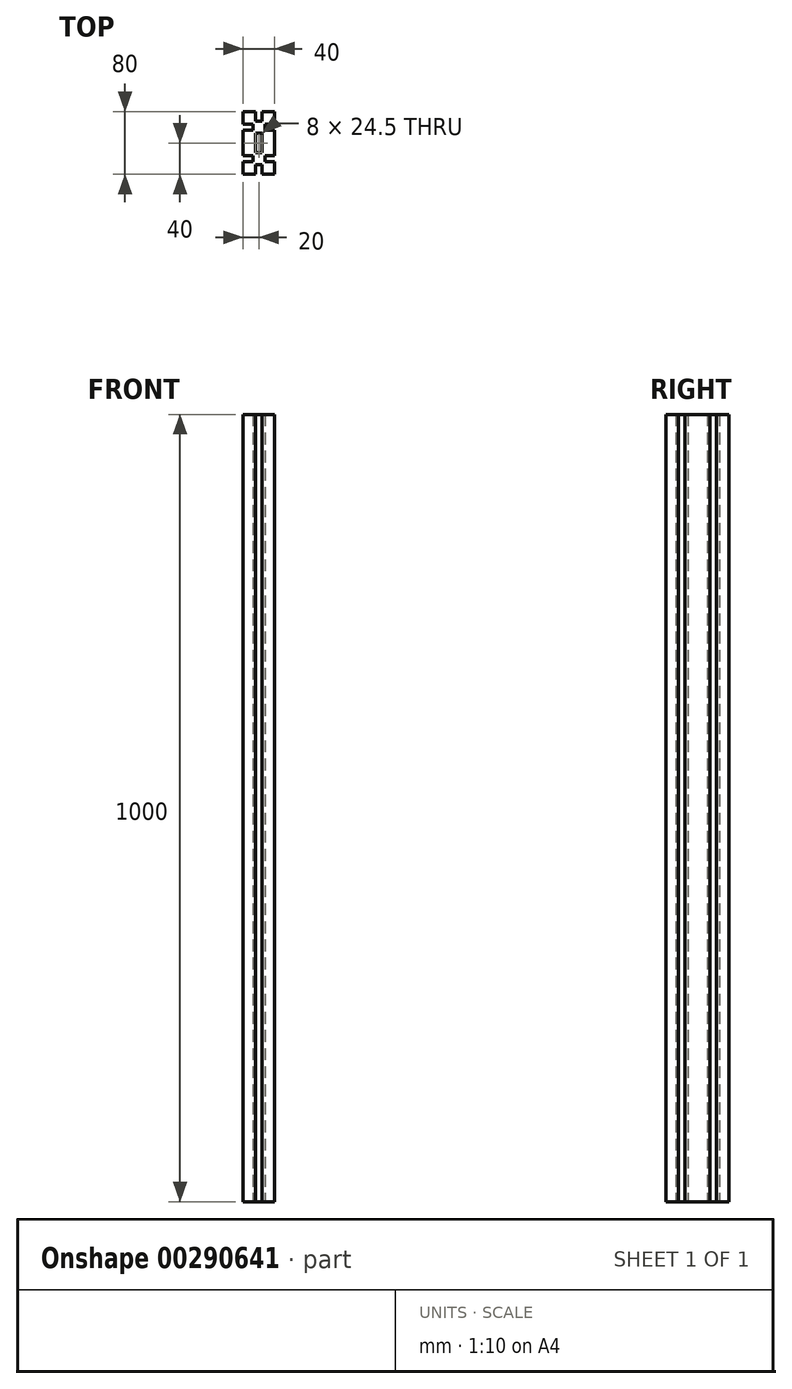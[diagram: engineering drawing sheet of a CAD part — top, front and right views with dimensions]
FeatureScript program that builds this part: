
annotation { "Feature Type Name" : "Feature", "Feature Type Description" : "" }
export const myFeature = defineFeature(function(context is Context, id is Id, definition is map)
    precondition{}
    {
        {
            var Q0;
            Q0=qCreatedBy(makeId("Top.planeOp"),FACE);
            var sketch = newSketch(context, id + "F0", { "sketchPlane" : qUnion([Q0])});
            skLineSegment(sketch, "E0.bottom", {"start": v(0, 0) * mm, "end": v(16, 0) * mm});
            skLineSegment(sketch, "E0.top", {"start": v(0, 40) * mm, "end": v(40, 40) * mm});
            skLineSegment(sketch, "E0.left", {"start": v(0, 0) * mm, "end": v(0, 40) * mm});
            skLineSegment(sketch, "E0.right", {"start": v(40, 0) * mm, "end": v(40, 40) * mm});
            skLineSegment(sketch, "E1.bottom", {"start": v(16, 40) * mm, "end": v(24, 40) * mm});
            skLineSegment(sketch, "E1.top", {"start": v(16, 27.75) * mm, "end": v(24, 27.75) * mm});
            skLineSegment(sketch, "E1.left", {"start": v(16, 40) * mm, "end": v(16, 27.75) * mm});
            skLineSegment(sketch, "E1.right", {"start": v(24, 40) * mm, "end": v(24, 27.75) * mm});
            skLineSegment(sketch, "E2.bottom", {"start": v(40, 24) * mm, "end": v(27.75, 24) * mm});
            skLineSegment(sketch, "E2.top", {"start": v(40, 16) * mm, "end": v(27.75, 16) * mm});
            skLineSegment(sketch, "E2.left", {"start": v(40, 24) * mm, "end": v(40, 16) * mm});
            skLineSegment(sketch, "E2.right", {"start": v(27.75, 24) * mm, "end": v(27.75, 16) * mm});
            skLineSegment(sketch, "E3.top", {"start": v(24, 12.25) * mm, "end": v(16, 12.25) * mm});
            skLineSegment(sketch, "E3.left", {"start": v(24, 0) * mm, "end": v(24, 12.25) * mm});
            skLineSegment(sketch, "E3.right", {"start": v(16, 0) * mm, "end": v(16, 12.25) * mm});
            skLineSegment(sketch, "E4.bottom", {"start": v(0, 16) * mm, "end": v(12.25, 16) * mm});
            skLineSegment(sketch, "E4.top", {"start": v(0, 24) * mm, "end": v(12.25, 24) * mm});
            skLineSegment(sketch, "E4.left", {"start": v(0, 16) * mm, "end": v(0, 24) * mm});
            skLineSegment(sketch, "E4.right", {"start": v(12.25, 16) * mm, "end": v(12.25, 24) * mm});
            skLineSegment(sketch, "E5.MirrorCS", {"start": v(12.25, -16) * mm, "end": v(12.25, -24) * mm});
            skLineSegment(sketch, "E6.MirrorCS", {"start": v(24, -12.25) * mm, "end": v(16, -12.25) * mm});
            skLineSegment(sketch, "E7.MirrorCS", {"start": v(24, 0) * mm, "end": v(24, -12.25) * mm});
            skLineSegment(sketch, "E8.MirrorCS", {"start": v(16, 0) * mm, "end": v(16, -12.25) * mm});
            skLineSegment(sketch, "E9.MirrorCS", {"start": v(0, -40) * mm, "end": v(40, -40) * mm});
            skLineSegment(sketch, "E10.MirrorCS", {"start": v(0, 0) * mm, "end": v(0, -40) * mm});
            skLineSegment(sketch, "E11.MirrorCS", {"start": v(40, 0) * mm, "end": v(40, -40) * mm});
            skLineSegment(sketch, "E12.MirrorCS", {"start": v(16, -40) * mm, "end": v(24, -40) * mm});
            skLineSegment(sketch, "E13.MirrorCS", {"start": v(16, -27.75) * mm, "end": v(24, -27.75) * mm});
            skLineSegment(sketch, "E14.MirrorCS", {"start": v(16, -40) * mm, "end": v(16, -27.75) * mm});
            skLineSegment(sketch, "E15.MirrorCS", {"start": v(24, -40) * mm, "end": v(24, -27.75) * mm});
            skLineSegment(sketch, "E16.MirrorCS", {"start": v(40, -24) * mm, "end": v(27.75, -24) * mm});
            skLineSegment(sketch, "E17.MirrorCS", {"start": v(40, -16) * mm, "end": v(27.75, -16) * mm});
            skLineSegment(sketch, "E18.MirrorCS", {"start": v(40, -24) * mm, "end": v(40, -16) * mm});
            skLineSegment(sketch, "E19.MirrorCS", {"start": v(27.75, -24) * mm, "end": v(27.75, -16) * mm});
            skLineSegment(sketch, "E20.MirrorCS", {"start": v(0, -16) * mm, "end": v(12.25, -16) * mm});
            skLineSegment(sketch, "E21.MirrorCS", {"start": v(0, -24) * mm, "end": v(12.25, -24) * mm});
            skLineSegment(sketch, "E22.MirrorCS", {"start": v(0, -16) * mm, "end": v(0, -24) * mm});
            skLineSegment(sketch, "E23.trimOffspring", {"start": v(24, 0) * mm, "end": v(40, 0) * mm});
            skSolve(sketch);
        }
        {
            var Q0;
            Q0=makeQuery(id+"F0.imprint","IMPRINT",FACE,{"disambiguationData":[TD([[makeQuery(id+"F0.imprint","IMPRINT",EDGE,{"derivedFrom":sQuery(id+"F0.wireOp",EDGE,"E1.top")}),-1.0]])]});
            var Q1;
            Q1=makeQuery(id+"F0.imprint","IMPRINT",FACE,{"disambiguationData":[TD([[makeQuery(id+"F0.imprint","IMPRINT",EDGE,{"derivedFrom":sQuery(id+"F0.wireOp",EDGE,"E5.MirrorCS")}),1.0]])]});
            extrude(context, id + "F1", {"entities" : qUnion([Q0, Q1]), "depth" : 1000 * mm});
        }
    });
